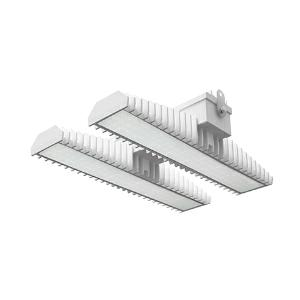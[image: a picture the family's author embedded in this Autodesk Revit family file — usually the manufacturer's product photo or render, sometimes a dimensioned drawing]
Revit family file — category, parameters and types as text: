
# Revit family: 3f_filippi_-_3f_lem_ho_medio_3f_filippi_-_58965_a0812_-_3f_lem_2_ho_led_140_cr_medio___vs_4eed
name_source: partatom
category: Lighting Fixtures
units: mm (PartAtom-declared; Revit-internal decimal feet)

## family parameters
Cut with Voids When Loaded = No
Host = Face
Light Source = No
Part Type = Normal
Room Calculation Point = No
Round Connector Dimension = Use Diameter
Shared = No

## types (1)
- 3F Filippi - 3F LEM HO Medio (1 x LED, 17918 lm, 138 W, 4000 K)
    Apparent Load = 138 VA
    Approval mark = CE
    CIE Flux Codes = 77 92 98 100 100
    Color Rendering = 80
    Color Temperature = 4000 K
    Control Gear = Electronic ballast
    Default Elevation = 1800 mm
    Description = Industrial luminaire with high light output and high luminous efficiency designed with the most innovative technologies for environments with temperature up to 55°C.

ILLUMINOTECHNICAL
Luminous efficiency 100% (DLOR 98%, ULOR 2%).
Initial luminous flux of the luminaire 17918 lm.
Medium distribution with rectangular shape.
Installation Interdistance Transv.D = 1.10 x hu - Long.D = 1.14 x hu.
Tabular UGR (CIE 117 - 4H-8H; S=0.25H; 70/50/20): RUG 21.5 - 21.4.
Beam angle: 58° - 57°.
Luminous efficacy 130 lm/W.
Lifetime (L93/B10): 30000 h. (tq+25°C)
Lifetime (L90/B10): 50000 h. (tq+25°C)
Lifetime (L85/B10): 80000 h. (tq+25°C)
Lifetime (L80/B10): 100000 h. (tq+25°C)
Lifetime (L85/B10): 50000 h. (tq+55°C)
Sudden decreased luminous flux after 50000 hours: 0% (C0).
Photobiological safety in compliance with IEC/TR 62778: RG0 risk exempt, (IEC 62471).
In compliance with IEC/EN 62722-2-1 - IEC/EN 62717 standards.

SOURCE
2 Mid-Power linear LED modules 70W/840.
Energy efficiency class (UE 2019/2020 - UE 2019/2015): C.
CIE 13.3 Colour rendering index: CRI >80 (R9 <50%).
IES TM-30 Fidelity Index: Rf = 84 Rg = 95.
CCT nominal colour temperature 4000 K.
Colour initial tolerance (MacAdam): SDCM 3.

MECHANICAL
Passive modular heatsinks in die-casted aluminium, painted in white colour.
To optimize the thermal management of the LED module, the heatsinks are oversized and provided with self-cleaning of cooling fins.
Wiring body in aluminium and galvanised steel anchored solidly to the sinks and thermally separated.
3F Lens lenses with high luminous efficiency, transparent methacrylate (PMMA), fixed to the LED modules.
Fixing brackets in stainless steel.
Luminaire with limited surface temperature. - D - (EN 60598-2-24)
Dimensions: 470x542 mm, height 133 mm. Weight 10.06 kg.
IP65 protection degree.
Mechanical strength to impacts IK06 (1 joule).
Glow-wire test resistance 650°C.

ELECTRICAL
Halogen Free electronic wiring 230V-50/60Hz, power factor 0.97, THD <25%, constant output current, class I, 1 driver.
Power of the luminaire 138 W.
ENEC - CE.
SAFE FLICKER: PstLM=<1 and SVM=<0.4 (IEC TR 61547-1 and IEC TR 63158), to ensure a more comfortable and safe light.
Luminaire compliant with EN 60598-2-22 for power supply from a centralised emergency system CPSS (Central Power Supply System), not incorporated in the luminaire - high risk areas excluded. The default power and flux are 100% in AC and 100% in DC.
Ambient temperature from -30°C to +55°C.
Temperature class T6 max 85°C.
Quick connection via M20 3P connector with 9-13 mm tightening range.
Power unit positioned on a separate compartment by the LED module to ensure optimum temperatures of cabling components, to be inspectable and maintainable.
Relative humidity UR: <85%.

INSTALLATION
Ceiling / Suspended / Wall.
All accessories dedicated to this product are available on the Catalog and on our website www.3F-Filippi.com.

ACCESSORIES
A0812 - Anti-glare microprismatic VS moulded glass, tempered, not flammable, with sealing gasket.
One required for each light module. The pack contains 10 pieces.

APPLICATIONS
In commercial environments, exhibition and industrial areas, stores, open areas.
Environments in which it is necessary a total protection against falling fragments (eg environments with foodstuffs or machines with moving parts or with extreme temperature changes), use luminaires with polycarbonate lenses.

WARNING
Fixture not suitable for cold stores with an ambient temperature <0°C and/or relative humidity >85%.
Luminaire designed for disposal/recycling at end-of-life.
Replaceable (LED only) light source by a professional. Replaceable control gear by a professional.
    Height = 133 mm
    Lamp = 1 x LED
    Lamp Light Flux = 17918 lm
    Lamp Power = 138 W
    Lamp count = 1
    Length = 470 mm
    Lifetime = 50000 h
    Luminous efficacy = 130 lm/W
    Manufacturer = 3F Filippi
    ModVariant = No
    Model = 3F Filippi - 58965+A0812 - 3F LEM 2 HO LED 140 CR MEDIO + VS
    Mounting Place = Ceiling
    Mounting Type = Pendant
    Number of Poles = 1
    OnlyDefault = Yes
    Power Factor = 1
    Product Name = 3F Filippi - 3F LEM HO Medio
    Product group = pendant luminaire
    ProductGroupID = 9
    Protection Class = Protection class I
    Protection Degree = IP 65
    RLX_Detail_Level = 1
    RLX_Emergency_Light_Flux = 0 lm
    RLX_Emergency_Type = 0
    RLX_Emergency_Type_DB = No
    RlxData = <blob elided: 95073 chars, md5=099787c9>
    Socket = socket
    Standby Power = 0 W
    System Light Flux = 17918 lm
    System Power = 138 W
    Type Comments = Product without accessories
    Type Image = 3f_filippi_-_lem_2__a0812.jpg
    URL = http://relux.com
    VarID = ---
    Voltage = 0 V
    Weight = 0.00 kg
    Width = 542 mm

## geometry (parser evidence)
native form markers: Blend x4, Sweep x11
no freeform markers — native parametric forms only
